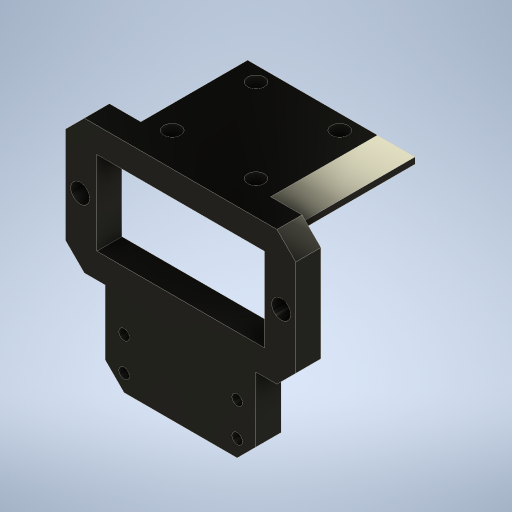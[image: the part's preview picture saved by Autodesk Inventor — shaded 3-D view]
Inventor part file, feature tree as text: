
AUTODESK INVENTOR PART (.ipt)
format: ipt  version: 2024.3 (Build 283343000, 343)  size: 324,096 bytes
history: native  units: mm
features: extrude x4, sketch x4, chamfer x3
ambient origin geometry x8: Origin, YZ Plane, XZ Plane, XY Plane, X Axis, Y Axis, Z Axis, Center Point
bodies: Solid1 (feature_tree)
feature tree (11):
  extrude  "Extrusion1"  Depth=20.0mm
  chamfer  "Chamfer1"  Distance=24.0mm
  extrude  "Extrusion3"  Depth=6.0mm TaperAngle=0.0deg
  chamfer  "Chamfer2"  Distance=2.0mm Angle=45.0deg
  extrude  "Extrusion4"  Depth=10.0mm
  chamfer  "Chamfer3"  Distance=10.0mm
  extrude  "Extrusion2"  Depth=20.0mm
  sketch  "Sketch1"  dims[d0=40.0mm d1=20.0mm]
  sketch  "Sketch2"  dims[d2=32.0mm]
  sketch  "Sketch3"  dims[d3=55.0mm]
  sketch  "Sketch6"  dims[d4=4.5mm d5=24.0mm d6=6.0mm d7=0.0mm d8=4.5mm d9=2.0mm d10=45.0deg d11=10.0mm d13=10.0mm d14=0.0mm d17=18.0mm d18=20.0mm d19=2.5mm d20=2.5mm d21=8.0mm d22=16.0mm d23=6.0mm d24=0.0mm d26=13.5mm d27=4.5mm d28=2.0mm d29=45.0deg d30=40.0mm d31=30.0mm d32=0.0mm d33=4.5mm d34=2.0mm d35=45.0deg d36=5.0mm d37=4.0mm d38=20.0mm d40=20.0mm d41=20.0mm d43=20.0mm d25=0.5mm]
